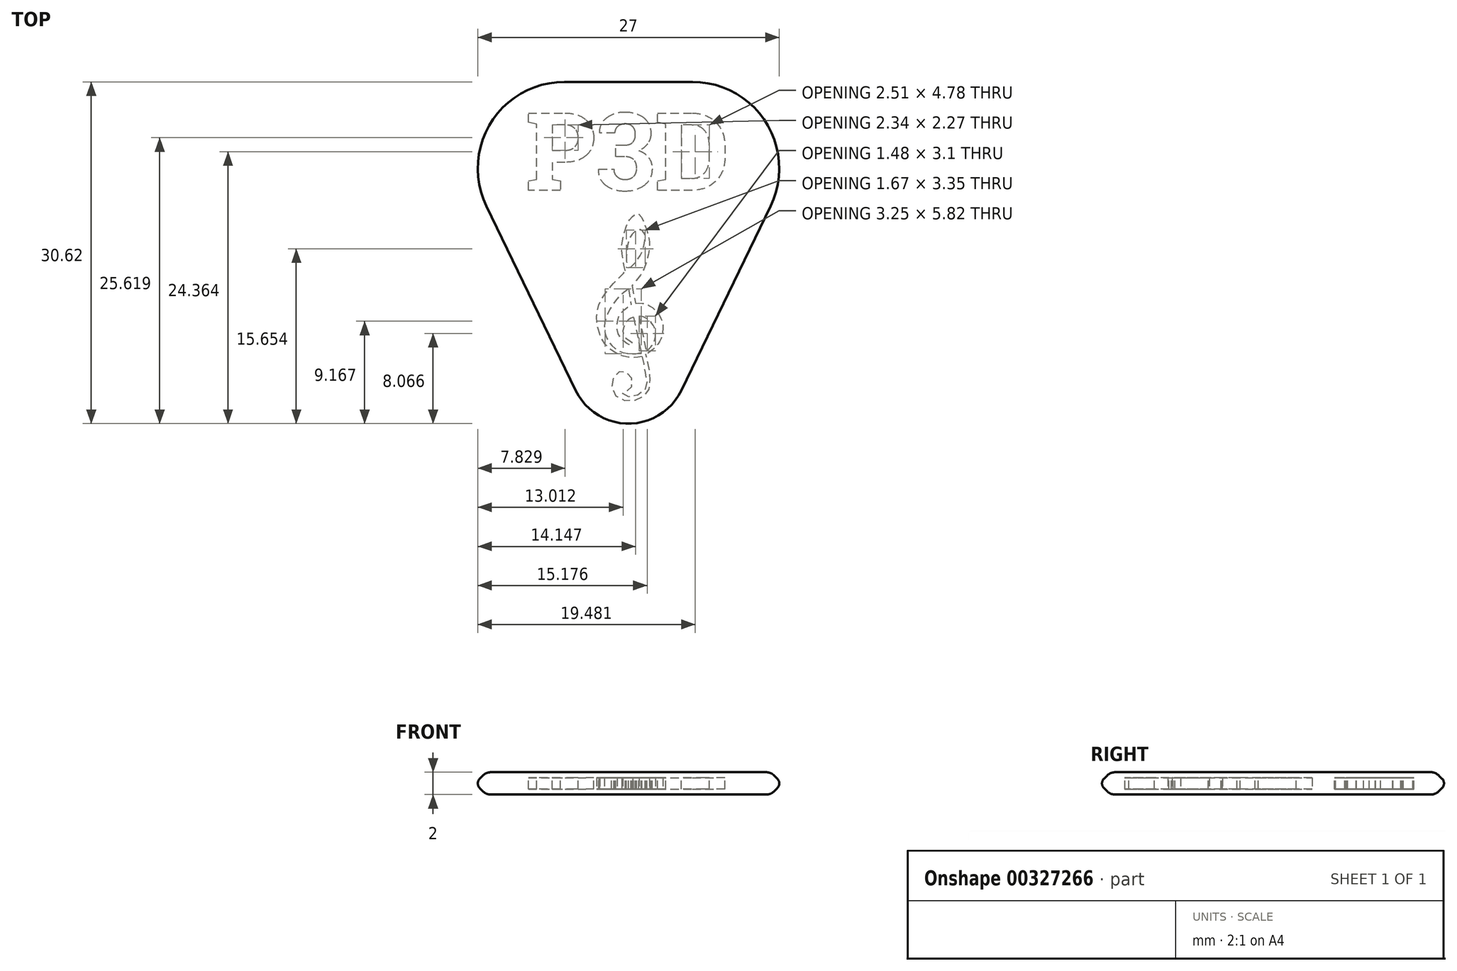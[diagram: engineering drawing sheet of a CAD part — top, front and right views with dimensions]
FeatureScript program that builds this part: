
annotation { "Feature Type Name" : "Feature", "Feature Type Description" : "" }
export const myFeature = defineFeature(function(context is Context, id is Id, definition is map)
    precondition{}
    {
        {
            var Q0;
            Q0=qCreatedBy(makeId("Top.planeOp"),FACE);
            var sketch = newSketch(context, id + "F0", { "sketchPlane" : qUnion([Q0])});
            skLineSegment(sketch, "E0", {"start": v(-5.74, 12.45) * mm, "end": v(5.74, 12.45) * mm});
            skLineSegment(sketch, "E1", {"start": v(12.95, 0.97) * mm, "end": v(4.95, -15.56) * mm});
            skLineSegment(sketch, "E2", {"start": v(-4.95, -15.56) * mm, "end": v(-12.95, 0.97) * mm});
            skPoint(sketch, "E3.visualSharp", {"position": v(-18.5, 12.45) * mm});
            skArc(sketch, "E3.filletArc", {"start": v(-5.74, 12.45) * mm, "mid": v(-12.52, 8.7) * mm, "end": v(-12.95, 0.97) * mm});
            skPoint(sketch, "E4.visualSharp", {"position": v(18.5, 12.45) * mm});
            skArc(sketch, "E4.filletArc", {"start": v(12.95, 0.97) * mm, "mid": v(12.52, 8.7) * mm, "end": v(5.74, 12.45) * mm});
            skPoint(sketch, "E5.visualSharp", {"position": v(0, -25.8) * mm});
            skArc(sketch, "E5.filletArc", {"start": v(-4.95, -15.56) * mm, "mid": v(0, -18.66) * mm, "end": v(4.95, -15.56) * mm});
            skSolve(sketch);
        }
        {
            var Q0;
            Q0=makeQuery(id+"F0.imprint","IMPRINT",FACE,{"disambiguationData":[TD([[makeQuery(id+"F0.imprint","IMPRINT",EDGE,{"derivedFrom":sQuery(id+"F0.wireOp",EDGE,"E0")}),-1.0]])]});
            extrude(context, id + "F1", {"entities" : qUnion([Q0]), "endBound" : BoundingType.SYMMETRIC, "depth" : 2 * mm});
        }
        {
            var Q0;
            Q0=makeQuery(id+"F1.opExtrude","CAP_EDGE",EDGE,{"disambiguationData":[OSD([sQuery(id+"F0.wireOp",EDGE,"E1")])],"isStart":false});
            var Q1;
            Q1=makeQuery(id+"F1.opExtrude","CAP_EDGE",EDGE,{"disambiguationData":[OSD([sQuery(id+"F0.wireOp",EDGE,"E1")])],"isStart":true});
            chamfer(context, id + "F2", {"entities" : qUnion([Q0, Q1]), "chamferType" : ChamferType.OFFSET_ANGLE, "width" : 1 * mm, "oppositeDirection" : false, "angle" : 45 * degree, "tangentPropagation" : true});
        }
        {
            var Q0;
            {var subQ0=sQuery(id+"F0.wireOp",EDGE,"E2");Q0=makeQuery(id+"F2.opChamfer","BLEND_EDGE",EDGE,{"blendedFrom":[makeQuery(id+"F1.opExtrude","CAP_EDGE",EDGE,{"disambiguationData":[OSD([subQ0])],"isStart":false}),makeQuery(id+"F1.opExtrude","CAP_FACE",FACE,{"disambiguationData":[OSD([sQuery(id+"F0.wireOp",EDGE,"E0"),sQuery(id+"F0.wireOp",EDGE,"E1"),subQ0,sQuery(id+"F0.wireOp",EDGE,"E3.filletArc"),sQuery(id+"F0.wireOp",EDGE,"E4.filletArc"),sQuery(id+"F0.wireOp",EDGE,"E5.filletArc")])],"isStart":false})],"blendedInto":[makeQuery(id+"F1.opExtrude","CAP_FACE",FACE,{"disambiguationData":[OSD([sQuery(id+"F0.wireOp",EDGE,"E0"),sQuery(id+"F0.wireOp",EDGE,"E1"),subQ0,sQuery(id+"F0.wireOp",EDGE,"E3.filletArc"),sQuery(id+"F0.wireOp",EDGE,"E4.filletArc"),sQuery(id+"F0.wireOp",EDGE,"E5.filletArc")])],"isStart":false})]});}
            var Q1;
            {var subQ0=sQuery(id+"F0.wireOp",EDGE,"E1");Q1=makeQuery(id+"F2.opChamfer","BLEND_EDGE",EDGE,{"blendedFrom":[makeQuery(id+"F1.opExtrude","CAP_EDGE",EDGE,{"disambiguationData":[OSD([subQ0])],"isStart":true}),makeQuery(id+"F1.opExtrude","CAP_FACE",FACE,{"disambiguationData":[OSD([sQuery(id+"F0.wireOp",EDGE,"E0"),subQ0,sQuery(id+"F0.wireOp",EDGE,"E2"),sQuery(id+"F0.wireOp",EDGE,"E3.filletArc"),sQuery(id+"F0.wireOp",EDGE,"E4.filletArc"),sQuery(id+"F0.wireOp",EDGE,"E5.filletArc")])],"isStart":true})],"blendedInto":[makeQuery(id+"F1.opExtrude","CAP_FACE",FACE,{"disambiguationData":[OSD([sQuery(id+"F0.wireOp",EDGE,"E0"),subQ0,sQuery(id+"F0.wireOp",EDGE,"E2"),sQuery(id+"F0.wireOp",EDGE,"E3.filletArc"),sQuery(id+"F0.wireOp",EDGE,"E4.filletArc"),sQuery(id+"F0.wireOp",EDGE,"E5.filletArc")])],"isStart":true})]});}
            fillet(context, id + "F3", {"entities" : qUnion([Q0, Q1]), "radius" : 1 * mm, "tangentPropagation" : true, "allowEdgeOverflow" : false});
        }
        {
            var Q0;
            Q0=qCreatedBy(makeId("Top.planeOp"),FACE);
            var sketch = newSketch(context, id + "F4", { "sketchPlane" : qUnion([Q0])});
            skText(sketch, "E6", { "text": "P3D", "fontName": "RobotoSlab-Bold.ttf"});
            const initialGuessF4  = {"E6": [-0.00923, 0.0025, 1, 0, 0.007]};
            skSetInitialGuess(sketch, initialGuessF4);
            skSolve(sketch);
        }
        {
            var Q0;
            Q0=qSketchRegion(id+"F4",true);
            extrude(context, id + "F5", {"entities" : qUnion([Q0]), "operationType" : NewBodyOperationType.REMOVE, "endBound" : BoundingType.SYMMETRIC, "oppositeDirection" : true, "depth" : 1 * mm, "offsetDistance" : 25 * mm});
        }
        {
            var Q0;
            {var subQ0=sQuery(id+"F0.wireOp",EDGE,"E2");Q0=makeQuery(id+"F2.opChamfer","BLEND_EDGE",EDGE,{"blendedFrom":[makeQuery(id+"F1.opExtrude","CAP_EDGE",EDGE,{"disambiguationData":[OSD([subQ0])],"isStart":true}),makeQuery(id+"F1.opExtrude","CAP_EDGE",EDGE,{"disambiguationData":[OSD([subQ0])],"isStart":false})],"blendedInto":[]});}
            fillet(context, id + "F6", {"entities" : qUnion([Q0]), "radius" : 0.6 * mm, "tangentPropagation" : true, "allowEdgeOverflow" : false});
        }
        {
            var Q0;
            Q0=qCreatedBy(makeId("Top.planeOp"),FACE);
            var sketch = newSketch(context, id + "F7", { "sketchPlane" : qUnion([Q0])});
            skFitSpline(sketch, "E7", {"points": [v(-0.3, -4.72) * mm, v(-0.52, -3.56) * mm, v(-0.6, -2.34) * mm, v(0, -0.3) * mm, v(0.41, 0.2) * mm, v(0.85, 0.4) * mm, v(1.28, -0.17) * mm, v(1.78, -1.6) * mm, v(1.84, -2.94) * mm, v(1.3, -4.7) * mm, v(0.3, -6.05) * mm], "startDerivative": vector(-2.37, 11.9) * mm, "endDerivative": vector(-9.26, -10.65) * mm});
            skFitSpline(sketch, "E8", {"points": [v(0, -6.33) * mm, v(-0.87, -7.06) * mm, v(-1.8, -8.37) * mm, v(-2.14, -9.5) * mm, v(-2.03, -10.56) * mm, v(-1.42, -11.5) * mm, v(-0.32, -12.08) * mm, v(0.72, -12.13) * mm, v(1.14, -12.04) * mm], "startDerivative": vector(-6.75, -4.93) * mm, "endDerivative": vector(4.6, 1.28) * mm});
            skFitSpline(sketch, "E9", {"points": [v(1.58, -11.9) * mm, v(2.17, -11.3) * mm, v(2.4, -10.2) * mm, v(1.93, -9.23) * mm, v(1.38, -8.87) * mm, v(0.94, -8.8) * mm], "startDerivative": vector(3.5, 2.41) * mm, "endDerivative": vector(-3.22, 0.24) * mm});
            skFitSpline(sketch, "E10", {"points": [v(0.43, -8.9) * mm, v(0, -9.1) * mm, v(-0.46, -9.84) * mm, v(-0.32, -10.67) * mm, v(0.36, -11.2) * mm, v(0.27, -11.36) * mm, v(-0.2, -11.2) * mm, v(-0.9, -10.42) * mm, v(-0.97, -9.13) * mm, v(-0.56, -8.38) * mm, v(0.22, -7.76) * mm], "startDerivative": vector(-5.47, -1.78) * mm, "endDerivative": vector(7.38, 5.22) * mm});
            skFitSpline(sketch, "E11", {"points": [v(0.62, -7.64) * mm, v(1.47, -7.67) * mm, v(2.02, -7.94) * mm, v(2.6, -8.5) * mm, v(3.04, -9.42) * mm, v(3.03, -10.39) * mm, v(2.74, -11.14) * mm, v(2.1, -11.85) * mm, v(1.56, -12.2) * mm], "startDerivative": vector(7.14, 0.27) * mm, "endDerivative": vector(-4.76, -2.66) * mm});
            skFitSpline(sketch, "E12", {"points": [v(1.2, -12.41) * mm, v(0.22, -12.5) * mm, v(-1.02, -12.16) * mm, v(-2.2, -11.14) * mm, v(-2.78, -9.61) * mm, v(-2.71, -7.96) * mm, v(-1.66, -6.21) * mm, v(-0.6, -5.1) * mm, v(-0.3, -4.72) * mm], "startDerivative": vector(-8.43, -1.8) * mm, "endDerivative": vector(3.27, 4.67) * mm});
            skFitSpline(sketch, "E13", {"points": [v(0, -4.43) * mm, v(0.94, -3.53) * mm, v(1.42, -2.34) * mm, v(1.4, -1.33) * mm, v(0.94, -1.02) * mm, v(0.22, -1.58) * mm, v(-0.16, -3.05) * mm, v(0, -4.43) * mm]});
            skFitSpline(sketch, "E14", {"points": [v(0, -6.33) * mm, v(0.22, -7.76) * mm], "startDerivative": vector(0.22, -1.42) * mm, "endDerivative": vector(0.22, -1.42) * mm});
            skFitSpline(sketch, "E15", {"points": [v(0.3, -6.05) * mm, v(0.62, -7.64) * mm], "startDerivative": vector(0.32, -1.58) * mm, "endDerivative": vector(0.32, -1.58) * mm});
            skFitSpline(sketch, "E16", {"points": [v(0.43, -8.9) * mm, v(1.14, -12.04) * mm], "startDerivative": vector(0.7, -3.14) * mm, "endDerivative": vector(0.7, -3.14) * mm});
            skFitSpline(sketch, "E17", {"points": [v(0.94, -8.8) * mm, v(1.58, -11.9) * mm], "startDerivative": vector(0.65, -3.1) * mm, "endDerivative": vector(0.65, -3.1) * mm});
            skFitSpline(sketch, "E18", {"points": [v(1.2, -12.41) * mm, v(1.36, -13.12) * mm, v(1.58, -14.32) * mm, v(1.58, -15.21) * mm, v(0.62, -15.95) * mm, v(-0.3, -15.9) * mm, v(-0.57, -15.63) * mm, v(-0.11, -15.55) * mm, v(0.36, -14.75) * mm, v(0, -13.95) * mm, v(-0.74, -13.75) * mm, v(-1.39, -14.37) * mm, v(-1.37, -15.58) * mm, v(-0.32, -16.35) * mm, v(1.1, -16.12) * mm, v(1.82, -15.43) * mm, v(1.93, -14.22) * mm, v(1.82, -13.32) * mm, v(1.56, -12.2) * mm], "startDerivative": vector(3.83, -13.68) * mm, "endDerivative": vector(-3.26, 19.32) * mm});
            skSolve(sketch);
        }
        {
            var Q0;
            Q0=qSketchRegion(id+"F7",true);
            var Q1;
            Q1=makeQuery(id+"F7.imprint","IMPRINT",FACE,{"disambiguationData":[TD([[makeQuery(id+"F7.imprint","IMPRINT",EDGE,{"derivedFrom":sQuery(id+"F7.wireOp",EDGE,"b4bf5cf7-47f6-4e07-859f-e1e6065c9dbf.0")}),-1.0]])]});
            var Q2;
            Q2=makeQuery(id+"F7.imprint","IMPRINT",FACE,{"disambiguationData":[TD([[makeQuery(id+"F7.imprint","IMPRINT",EDGE,{"derivedFrom":sQuery(id+"F7.wireOp",EDGE,"6f85d2ec-8929-457e-84c4-58013a10ac05.0")}),-1.0]])]});
            extrude(context, id + "F8", {"entities" : qUnion([Q0, Q1, Q2]), "operationType" : NewBodyOperationType.REMOVE, "endBound" : BoundingType.SYMMETRIC, "oppositeDirection" : true, "depth" : 1 * mm, "offsetDistance" : 25 * mm});
        }
    });
